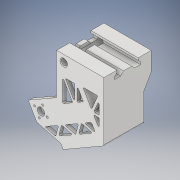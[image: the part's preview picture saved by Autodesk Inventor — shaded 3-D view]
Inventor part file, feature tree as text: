
AUTODESK INVENTOR PART (.ipt)
format: ipt  version: 2019 (Build 230136000, 136)  size: 528,896 bytes
history: native  units: in
note: dims shown in document units (in); Inventor stores cm internally (conversion verified against a paired STEP export)
features: extrude x10, sketch x10, projected_geometry x5, fillet x3, chamfer x2, hole x1
ambient origin geometry x8: Origin, YZ Plane, XZ Plane, XY Plane, X Axis, Y Axis, Z Axis, Center Point
bodies: Solid1 (feature_tree)
feature tree (31):
  extrude  "Extrusion1"  Depth=2.0in
  extrude  "Extrusion3"  Depth=2.0in
  extrude  "Extrusion4"  Depth=0.2in
  extrude  "Extrusion5"  TaperAngle=135.0deg  [1 undecoded]
  extrude  "Extrusion8"  Depth=0.45in
  extrude  "Extrusion9"  Depth=0.125in
  sketch  "Sketch11"  dims[d27=0.55in d28=0.25in]
  extrude  "Extrusion10"  Depth=0.25in
  hole  "Hole3"  [1 undecoded]
  chamfer  "Chamfer1"  Distance=1.6in
  extrude  "Extrusion14"  Depth=0.1285in TaperAngle=0.0deg
  fillet  "Fillet1"  Radius=0.1285in
  extrude  "Extrusion15"  Depth=0.2in
  extrude  "Extrusion16"  Depth=0.2in
  fillet  "Fillet2"  Radius=0.82in
  fillet  "Fillet3"  Radius=0.5in
  chamfer  "Chamfer3"  Distance=0.875in
  sketch  "Sketch1"  dims[d0=30.0deg d1=2.0in]
  sketch  "Sketch5"  dims[d2=3.5in d3=2.0in]
  projected_geometry  "Projected Loop2"
  sketch  "Sketch6"  dims[d4=0.2in d5=0.75in]
  projected_geometry  "Projected Loop3"
  sketch  "Sketch7"  dims[d6=2.0in d7=0.0in d22=135.0deg]
  sketch  "Sketch9"  dims[d23=0.45in d24=0.0922in]
  projected_geometry  "Projected Loop5"
  sketch  "Sketch10"  dims[d25=0.1in d26=0.125in]
  projected_geometry  "Projected Loop6"
  sketch  "Sketch16"  dims[d29=1.6in d30=0.0in d32=0.257in d33=1.6in d34=0.0in]
  sketch  "Sketch17"  dims[d35=0.3in d36=1.6in d37=0.0in d39=0.1285in]
  sketch  "Sketch18"  dims[d51=0.2in d52=0.2in d53=0.2in d54=0.82in d55=0.5in d56=0.875in d57=0.0625in d58=0.0625in d59=0.25in d60=0.75in d61=1.6in d62=0.0in d63=0.877in d64=1.0in d65=0.0in d66=0.15in d67=0.0in d86=0.315in d87=0.5512in d90=0.2in d91=0.2in d92=0.0827in d93=0.75in d94=0.375in d95=0.25in d96=0.5635in d97=1.0in d98=0.8108in d104=0.2in d105=0.1875in d106=0.125in d107=45.0deg d108=0.1in d109=0.2in d110=45.0deg d112=0.5in d114=0.25in d115=1.67in d116=0.3125in d117=1.0in d118=0.0in d119=0.688in d120=1.0in d121=0.0in d122=0.04in d123=0.05in d124=0.05in d125=0.05in d126=0.1in d127=45.0deg d128=0.1in d129=0.04in d131=0.25in d132=1.0in d133=0.0in d134=0.0312in d135=0.0312in d136=0.0625in d140=0.0312in d141=0.125in d142=45.0deg]
  projected_geometry  "Projected Loop8"
note: 2 required parameter values undecoded (feature->parameter linkage not recoverable at this tier; creation-order binding heuristic only, values carry confidence <= 0.55)
